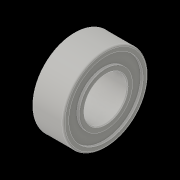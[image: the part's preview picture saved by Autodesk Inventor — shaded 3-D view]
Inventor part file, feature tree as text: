
AUTODESK INVENTOR PART (.ipt)
format: ipt  version: 2016 (Build 200138000, 138)  size: 145,920 bytes
history: native  units: in
note: dims shown in document units (in); Inventor stores cm internally (conversion verified against a paired STEP export)
features: chamfer x1
ambient origin geometry x8: Origin, YZ Plane, XZ Plane, XY Plane, X Axis, Y Axis, Z Axis, Center Point
bodies: Solid1 (feature_tree)
feature tree (1):
  chamfer  "Chamfer1"  [1 undecoded]
note: 1 required parameter value undecoded (feature->parameter linkage not recoverable at this tier; creation-order binding heuristic only, values carry confidence <= 0.55)
